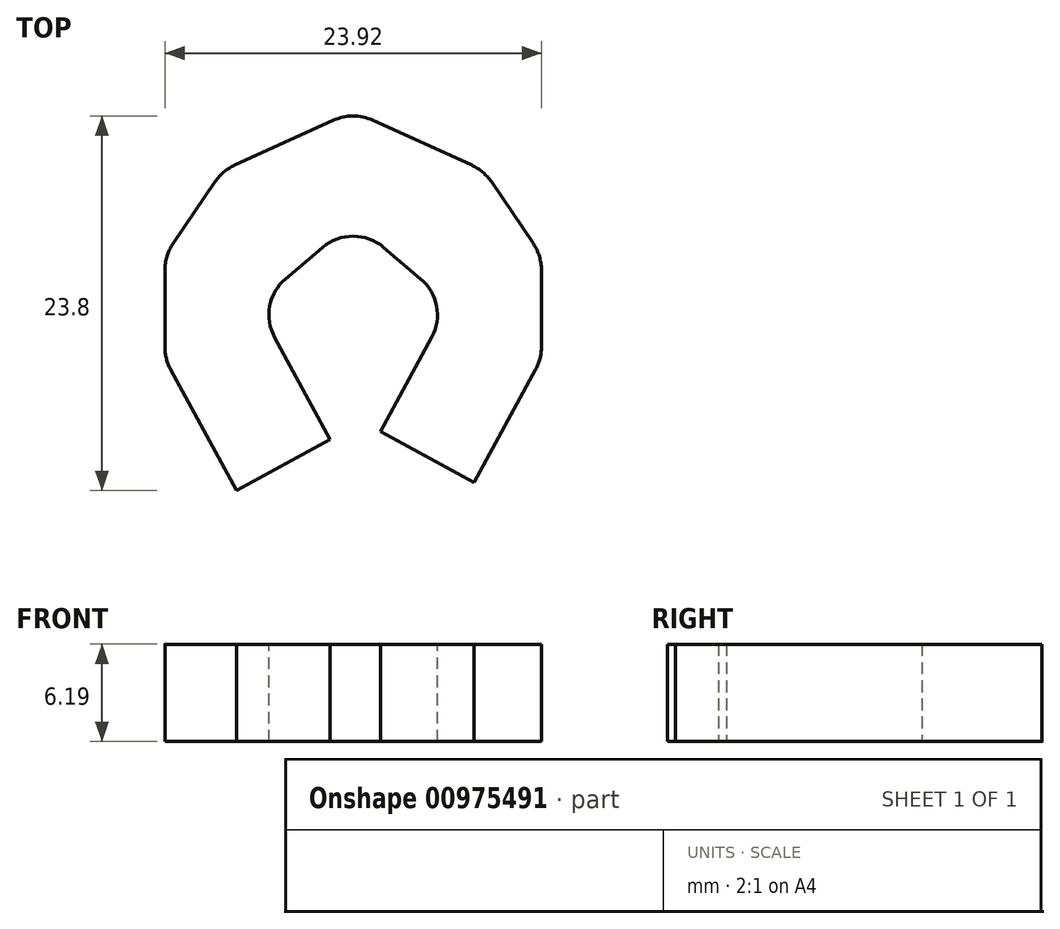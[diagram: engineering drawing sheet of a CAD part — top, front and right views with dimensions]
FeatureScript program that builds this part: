
annotation { "Feature Type Name" : "Feature", "Feature Type Description" : "" }
export const myFeature = defineFeature(function(context is Context, id is Id, definition is map)
    precondition{}
    {
        {
            var Q0;
            Q0=qCreatedBy(makeId("Top.planeOp"),FACE);
            var sketch = newSketch(context, id + "F0", { "sketchPlane" : qUnion([Q0])});
            skLineSegment(sketch, "E0", {"start": v(0, 40.51) * mm, "end": v(0, -38.65) * mm, "construction": true});
            skLineSegment(sketch, "E1", {"start": v(0, 40.51) * mm, "end": v(-8.3, 36.73) * mm});
            skLineSegment(sketch, "E2", {"start": v(-8.3, 36.73) * mm, "end": v(-11.96, 31.35) * mm});
            skLineSegment(sketch, "E3", {"start": v(-11.96, 31.35) * mm, "end": v(-11.96, 24.78) * mm});
            skLineSegment(sketch, "E4", {"start": v(-11.96, 24.78) * mm, "end": v(-8.86, 19.08) * mm});
            skLineSegment(sketch, "E5", {"start": v(-8.86, 19.08) * mm, "end": v(-2.9, 22.32) * mm});
            skLineSegment(sketch, "E6", {"start": v(-2.9, 22.32) * mm, "end": v(-6.15, 28.3) * mm});
            skLineSegment(sketch, "E7", {"start": v(-6.15, 28.3) * mm, "end": v(0, 33.51) * mm});
            skLineSegment(sketch, "E8.MirrorCS", {"start": v(0, 40.51) * mm, "end": v(8.3, 36.73) * mm});
            skLineSegment(sketch, "E9.MirrorCS", {"start": v(6.15, 28.3) * mm, "end": v(0, 33.51) * mm});
            skLineSegment(sketch, "E10.MirrorCS", {"start": v(2.9, 22.32) * mm, "end": v(6.15, 28.3) * mm});
            skLineSegment(sketch, "E11.MirrorCS", {"start": v(8.86, 19.08) * mm, "end": v(2.9, 22.32) * mm});
            skLineSegment(sketch, "E12.MirrorCS", {"start": v(11.96, 24.78) * mm, "end": v(8.86, 19.08) * mm});
            skLineSegment(sketch, "E13.MirrorCS", {"start": v(11.96, 31.35) * mm, "end": v(11.96, 24.78) * mm});
            skLineSegment(sketch, "E14.MirrorCS", {"start": v(8.3, 36.73) * mm, "end": v(11.96, 31.35) * mm});
            skSolve(sketch);
        }
        {
            var Q0;
            Q0=makeQuery(id+"F0.imprint","IMPRINT",FACE,{"disambiguationData":[TD([[makeQuery(id+"F0.imprint","IMPRINT",EDGE,{"derivedFrom":sQuery(id+"F0.wireOp",EDGE,"E1")}),1.0]])]});
            extrude(context, id + "F1", {"entities" : qUnion([Q0]), "depth" : 6.2 * mm, "offsetDistance" : 25 * mm});
        }
        {
            var Q0;
            Q0=makeQuery(id+"F1.opExtrude","SWEPT_EDGE",EDGE,{"disambiguationData":[OSD([sQuery(id+"F0.wireOp",EDGE,"E3"),sQuery(id+"F0.wireOp",EDGE,"E4")])]});
            var Q1;
            Q1=makeQuery(id+"F1.opExtrude","SWEPT_EDGE",EDGE,{"disambiguationData":[OSD([sQuery(id+"F0.wireOp",EDGE,"E1"),sQuery(id+"F0.wireOp",EDGE,"E8.MirrorCS")])]});
            var Q2;
            Q2=makeQuery(id+"F1.opExtrude","SWEPT_EDGE",EDGE,{"disambiguationData":[OSD([sQuery(id+"F0.wireOp",EDGE,"E13.MirrorCS"),sQuery(id+"F0.wireOp",EDGE,"E14.MirrorCS")])]});
            var Q3;
            Q3=makeQuery(id+"F1.opExtrude","SWEPT_EDGE",EDGE,{"disambiguationData":[OSD([sQuery(id+"F0.wireOp",EDGE,"E2"),sQuery(id+"F0.wireOp",EDGE,"E3")])]});
            var Q4;
            Q4=makeQuery(id+"F1.opExtrude","SWEPT_EDGE",EDGE,{"disambiguationData":[OSD([sQuery(id+"F0.wireOp",EDGE,"E9.MirrorCS"),sQuery(id+"F0.wireOp",EDGE,"E10.MirrorCS")])]});
            var Q5;
            Q5=makeQuery(id+"F1.opExtrude","SWEPT_EDGE",EDGE,{"disambiguationData":[OSD([sQuery(id+"F0.wireOp",EDGE,"E8.MirrorCS"),sQuery(id+"F0.wireOp",EDGE,"E14.MirrorCS")])]});
            var Q6;
            Q6=makeQuery(id+"F1.opExtrude","SWEPT_EDGE",EDGE,{"disambiguationData":[OSD([sQuery(id+"F0.wireOp",EDGE,"E1"),sQuery(id+"F0.wireOp",EDGE,"E2")])]});
            var Q7;
            Q7=makeQuery(id+"F1.opExtrude","SWEPT_EDGE",EDGE,{"disambiguationData":[OSD([sQuery(id+"F0.wireOp",EDGE,"E7"),sQuery(id+"F0.wireOp",EDGE,"E9.MirrorCS")])]});
            var Q8;
            Q8=makeQuery(id+"F1.opExtrude","SWEPT_EDGE",EDGE,{"disambiguationData":[OSD([sQuery(id+"F0.wireOp",EDGE,"E12.MirrorCS"),sQuery(id+"F0.wireOp",EDGE,"E13.MirrorCS")])]});
            var Q9;
            Q9=makeQuery(id+"F1.opExtrude","SWEPT_EDGE",EDGE,{"disambiguationData":[OSD([sQuery(id+"F0.wireOp",EDGE,"E6"),sQuery(id+"F0.wireOp",EDGE,"E7")])]});
            fillet(context, id + "F2", {"entities" : qUnion([Q0, Q1, Q2, Q3, Q4, Q5, Q6, Q7, Q8, Q9]), "radius" : 3 * mm, "tangentPropagation" : true, "allowEdgeOverflow" : false});
        }
        {
            var Q0;
            Q0=makeQuery(id+"F1.opExtrude","SWEPT_FACE",FACE,{"disambiguationData":[OSD([sQuery(id+"F0.wireOp",EDGE,"E11.MirrorCS")])]});
            extrude(context, id + "F3", {"entities" : qUnion([Q0]), "operationType" : NewBodyOperationType.ADD, "depth" : 2.44 * mm, "offsetDistance" : 25 * mm});
        }
        {
            var Q0;
            Q0=makeQuery(id+"F1.opExtrude","SWEPT_FACE",FACE,{"disambiguationData":[OSD([sQuery(id+"F0.wireOp",EDGE,"E5")])]});
            extrude(context, id + "F4", {"entities" : qUnion([Q0]), "operationType" : NewBodyOperationType.ADD, "depth" : 3.02 * mm, "offsetDistance" : 25 * mm});
        }
    });
